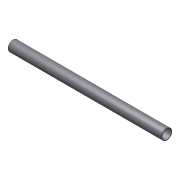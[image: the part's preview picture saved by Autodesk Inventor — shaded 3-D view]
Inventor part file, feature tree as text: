
AUTODESK INVENTOR PART (.ipt)
format: ipt  version: 2012 (Build 160160000, 160)  size: 107,520 bytes
history: native  units: in
note: dims shown in document units (in); Inventor stores cm internally (conversion verified against a paired STEP export)
features: other x42, revolve x1, sketch x1
ambient origin geometry x8: Origin, YZ Plane, XZ Plane, XY Plane, X Axis, Y Axis, Z Axis, Center Point
bodies: Solid1 (feature_tree)
feature tree (44):
  revolve  "Revolution1"  [1 undecoded]
  other  "tube_front_XY"
  other  "tube_front_YZ"
  other  "tube_front_ZX"
  other  "tube_front_X"
  other  "tube_front_Y"
  other  "tube_front_Z"
  other  "tube_front_Center"
  other  "tube_rear_XY"
  other  "tube_rear_YZ"
  other  "tube_rear_ZX"
  other  "tube_rear_X"
  other  "tube_rear_Y"
  other  "tube_rear_Z"
  other  "tube_rear_Center"
  other  "cp1_XY"
  other  "cp1_YZ"
  other  "cp1_ZX"
  other  "cp1_X"
  other  "cp1_Y"
  other  "cp1_Z"
  other  "cp1_Center"
  other  "cp2_XY"
  other  "cp2_YZ"
  other  "cp2_ZX"
  other  "cp2_X"
  other  "cp2_Y"
  other  "cp2_Z"
  other  "cp2_Center"
  other  "cp3_XY"
  other  "cp3_YZ"
  other  "cp3_ZX"
  other  "cp3_X"
  other  "cp3_Y"
  other  "cp3_Z"
  other  "cp3_Center"
  other  "cp4_XY"
  other  "cp4_YZ"
  other  "cp4_ZX"
  other  "cp4_X"
  other  "cp4_Y"
  other  "cp4_Z"
  other  "cp4_Center"
  sketch  "Sketch_1"  dims[d0=360.0deg]
note: 1 required parameter value undecoded (feature->parameter linkage not recoverable at this tier; creation-order binding heuristic only, values carry confidence <= 0.55)
